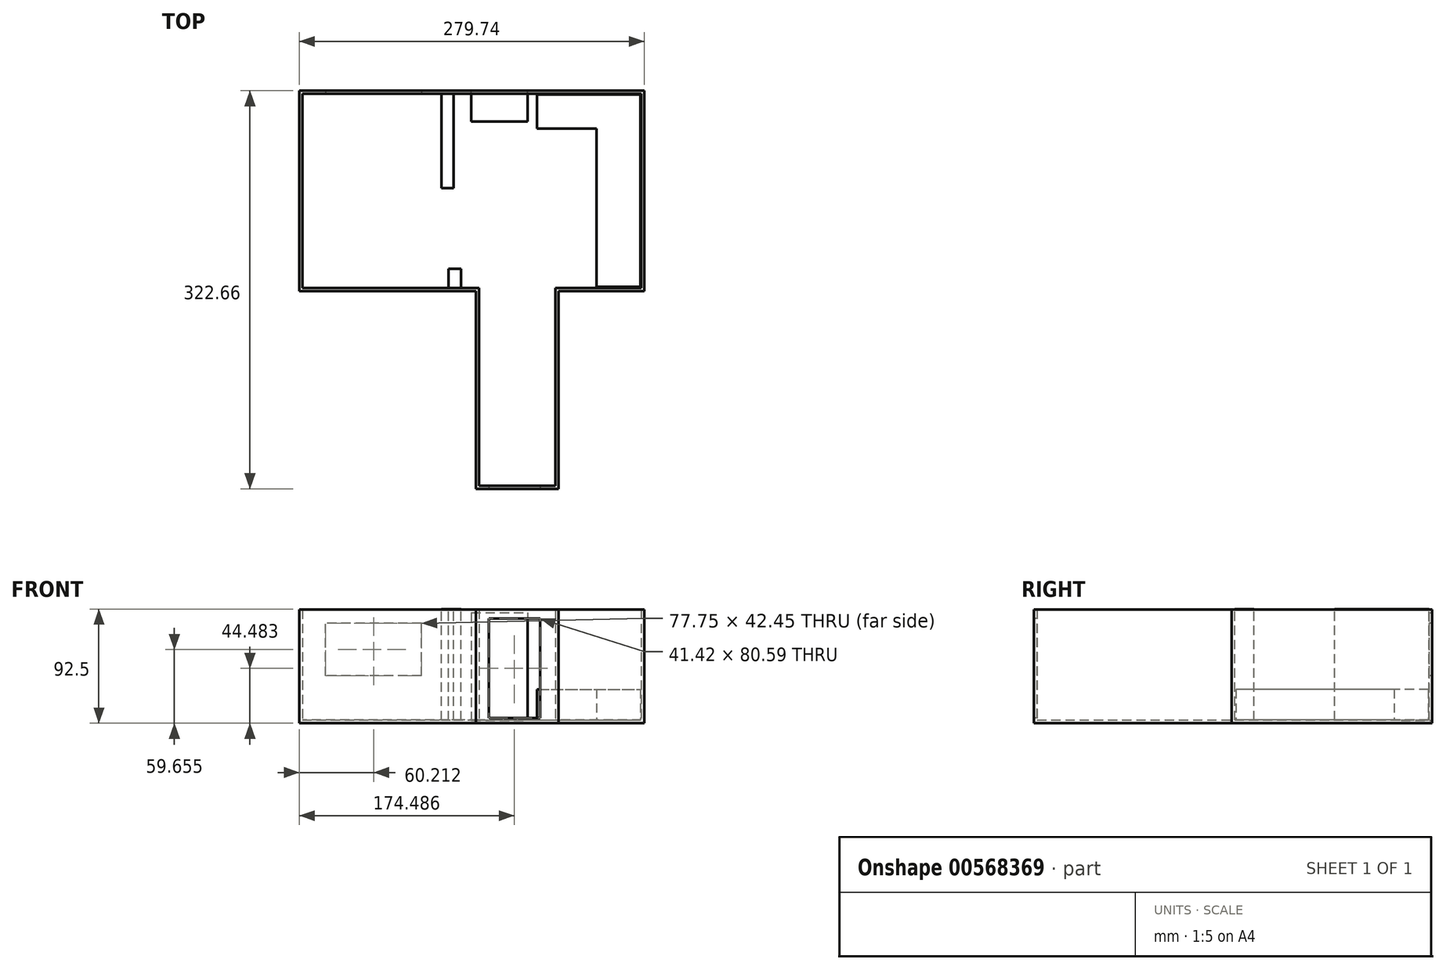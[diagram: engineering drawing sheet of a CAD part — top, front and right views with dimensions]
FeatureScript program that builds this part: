
annotation { "Feature Type Name" : "Feature", "Feature Type Description" : "" }
export const myFeature = defineFeature(function(context is Context, id is Id, definition is map)
    precondition{}
    {
        {
            var Q0;
            Q0=qCreatedBy(makeId("Top.planeOp"),FACE);
            var sketch = newSketch(context, id + "F0", { "sketchPlane" : qUnion([Q0])});
            skLineSegment(sketch, "E0", {"start": v(22.1, -110.4) * mm, "end": v(89.03, -110.4) * mm});
            skLineSegment(sketch, "E1", {"start": v(22.1, -110.4) * mm, "end": v(22.1, 49.82) * mm});
            skLineSegment(sketch, "E2", {"start": v(22.1, 49.82) * mm, "end": v(0, 49.82) * mm});
            skLineSegment(sketch, "E3", {"start": v(0, 49.82) * mm, "end": v(0, 72.95) * mm});
            skLineSegment(sketch, "E4", {"start": v(0, 49.82) * mm, "end": v(-121.09, 49.82) * mm});
            skLineSegment(sketch, "E5", {"start": v(-121.09, 49.82) * mm, "end": v(-121.09, 212.26) * mm});
            skLineSegment(sketch, "E6", {"start": v(-121.09, 212.26) * mm, "end": v(0, 212.26) * mm});
            skLineSegment(sketch, "E7", {"start": v(0, 212.26) * mm, "end": v(0, 116.46) * mm});
            skLineSegment(sketch, "E8", {"start": v(0, 212.26) * mm, "end": v(158.65, 212.26) * mm});
            skLineSegment(sketch, "E9", {"start": v(158.65, 212.26) * mm, "end": v(158.65, 49.82) * mm});
            skLineSegment(sketch, "E10", {"start": v(158.65, 49.82) * mm, "end": v(89.03, 49.82) * mm});
            skLineSegment(sketch, "E11", {"start": v(89.03, -110.4) * mm, "end": v(89.03, 49.82) * mm});
            skSolve(sketch);
        }
        {
            var Q0;
            Q0=makeQuery(id+"F0.imprint","IMPRINT",FACE,{"disambiguationData":[TD([[makeQuery(id+"F0.imprint","IMPRINT",EDGE,{"derivedFrom":sQuery(id+"F0.wireOp",EDGE,"E0")}),1.0]])]});
            extrude(context, id + "F1", {"entities" : qUnion([Q0]), "depth" : 92 * mm, "offsetDistance" : 25 * mm});
        }
        {
            var Q0;
            Q0=makeQuery(id+"F1.opExtrude","CAP_FACE",FACE,{"disambiguationData":[OSD([sQuery(id+"F0.wireOp",EDGE,"E0"),sQuery(id+"F0.wireOp",EDGE,"E1"),sQuery(id+"F0.wireOp",EDGE,"E2"),sQuery(id+"F0.wireOp",EDGE,"E4"),sQuery(id+"F0.wireOp",EDGE,"E5"),sQuery(id+"F0.wireOp",EDGE,"E6"),sQuery(id+"F0.wireOp",EDGE,"E8"),sQuery(id+"F0.wireOp",EDGE,"E9"),sQuery(id+"F0.wireOp",EDGE,"E10"),sQuery(id+"F0.wireOp",EDGE,"E11")])],"isStart":false});
            shell(context, id + "F2", {"entities" : qUnion([Q0]), "thickness" : 2.5 * mm});
        }
        {
            var Q0;
            Q0=makeQuery(id+"F2.opShell","OFFSET_FACE",FACE,{"disambiguationData":[OSD([sQuery(id+"F0.wireOp",EDGE,"E0"),sQuery(id+"F0.wireOp",EDGE,"E1"),sQuery(id+"F0.wireOp",EDGE,"E2"),sQuery(id+"F0.wireOp",EDGE,"E4"),sQuery(id+"F0.wireOp",EDGE,"E5"),sQuery(id+"F0.wireOp",EDGE,"E6"),sQuery(id+"F0.wireOp",EDGE,"E8"),sQuery(id+"F0.wireOp",EDGE,"E9"),sQuery(id+"F0.wireOp",EDGE,"E10"),sQuery(id+"F0.wireOp",EDGE,"E11")])]});
            var sketch = newSketch(context, id + "F3", { "sketchPlane" : qUnion([Q0])});
            skLineSegment(sketch, "E12", {"start": v(4.04, 52.32) * mm, "end": v(4.04, 89.94) * mm});
            skLineSegment(sketch, "E13", {"start": v(4.04, 209.76) * mm, "end": v(4.04, 133.28) * mm});
            skSolve(sketch);
        }
        {
            var Q0;
            Q0=sQuery(id+"F3.wireOp",EDGE,"E13");
            extrude(context, id + "F4", {"bodyType" : ToolBodyType.SURFACE, "surfaceEntities" : qUnion([Q0]), "depth" : 90 * mm, "offsetDistance" : 25 * mm});
        }
        {
            var Q0;
            Q0=makeQuery(id+"F4.opExtrude","SWEPT_FACE",FACE,{"disambiguationData":[OSD([sQuery(id+"F3.wireOp",EDGE,"E13")])]});
            extrude(context, id + "F5", {"entities" : qUnion([Q0]), "operationType" : NewBodyOperationType.ADD, "depth" : 10 * mm, "offsetDistance" : 25 * mm});
        }
        {
            var Q0;
            Q0=makeQuery(id+"F2.opShell","OFFSET_FACE",FACE,{"disambiguationData":[OSD([sQuery(id+"F0.wireOp",EDGE,"E0"),sQuery(id+"F0.wireOp",EDGE,"E1"),sQuery(id+"F0.wireOp",EDGE,"E2"),sQuery(id+"F0.wireOp",EDGE,"E4"),sQuery(id+"F0.wireOp",EDGE,"E5"),sQuery(id+"F0.wireOp",EDGE,"E6"),sQuery(id+"F0.wireOp",EDGE,"E8"),sQuery(id+"F0.wireOp",EDGE,"E9"),sQuery(id+"F0.wireOp",EDGE,"E10"),sQuery(id+"F0.wireOp",EDGE,"E11")])]});
            var sketch = newSketch(context, id + "F6", { "sketchPlane" : qUnion([Q0])});
            skLineSegment(sketch, "E14", {"start": v(0, 52.32) * mm, "end": v(0, 67.85) * mm});
            skSolve(sketch);
        }
        {
            var Q0;
            Q0=sQuery(id+"F6.wireOp",EDGE,"E14");
            extrude(context, id + "F7", {"bodyType" : ToolBodyType.SURFACE, "surfaceEntities" : qUnion([Q0]), "depth" : 90 * mm, "offsetDistance" : 25 * mm});
        }
        {
            var Q0;
            Q0=makeQuery(id+"F7.opExtrude","SWEPT_FACE",FACE,{"disambiguationData":[OSD([sQuery(id+"F6.wireOp",EDGE,"E14")])]});
            extrude(context, id + "F8", {"entities" : qUnion([Q0]), "operationType" : NewBodyOperationType.ADD, "depth" : 10 * mm, "offsetDistance" : 25 * mm});
        }
        {
            var Q0;
            Q0=makeQuery(id+"F1.opExtrude","SWEPT_FACE",FACE,{"disambiguationData":[OSD([sQuery(id+"F0.wireOp",EDGE,"E0")])]});
            var sketch = newSketch(context, id + "F9", { "sketchPlane" : qUnion([Q0])});
            skLineSegment(sketch, "E15", {"start": v(32.69, 84.78) * mm, "end": v(32.69, 4.19) * mm});
            skLineSegment(sketch, "E16", {"start": v(32.69, 4.19) * mm, "end": v(74.1, 4.19) * mm});
            skLineSegment(sketch, "E17", {"start": v(74.1, 4.19) * mm, "end": v(74.1, 84.78) * mm});
            skLineSegment(sketch, "E18", {"start": v(74.1, 84.78) * mm, "end": v(32.69, 84.78) * mm});
            skSolve(sketch);
        }
        {
            var Q0;
            Q0=makeQuery(id+"F9.imprint","IMPRINT",FACE,{"disambiguationData":[TD([[makeQuery(id+"F9.imprint","IMPRINT",EDGE,{"derivedFrom":sQuery(id+"F9.wireOp",EDGE,"E15")}),1.0]])]});
            extrude(context, id + "F10", {"entities" : qUnion([Q0]), "operationType" : NewBodyOperationType.REMOVE, "oppositeDirection" : true, "depth" : 25 * mm, "offsetDistance" : 25 * mm});
        }
        {
            var Q0;
            Q0=makeQuery(id+"F2.opShell","OFFSET_FACE",FACE,{"disambiguationData":[OSD([sQuery(id+"F0.wireOp",EDGE,"E0"),sQuery(id+"F0.wireOp",EDGE,"E1"),sQuery(id+"F0.wireOp",EDGE,"E2"),sQuery(id+"F0.wireOp",EDGE,"E4"),sQuery(id+"F0.wireOp",EDGE,"E5"),sQuery(id+"F0.wireOp",EDGE,"E6"),sQuery(id+"F0.wireOp",EDGE,"E8"),sQuery(id+"F0.wireOp",EDGE,"E9"),sQuery(id+"F0.wireOp",EDGE,"E10"),sQuery(id+"F0.wireOp",EDGE,"E11")])]});
            var sketch = newSketch(context, id + "F11", { "sketchPlane" : qUnion([Q0])});
            skPoint(sketch, "E19.0", {"position": v(-121.09, 212.26) * mm});
            skPoint(sketch, "E20.0", {"position": v(158.65, 212.26) * mm});
            skSolve(sketch);
        }
        {
            var Q0;
            Q0=makeQuery(id+"F1.opExtrude","SWEPT_FACE",FACE,{"disambiguationData":[OSD([sQuery(id+"F0.wireOp",EDGE,"E6"),sQuery(id+"F0.wireOp",EDGE,"E8")])]});
            var sketch = newSketch(context, id + "F12", { "sketchPlane" : qUnion([Q0])});
            skLineSegment(sketch, "E21.bottom", {"start": v(-18.47, 89.66) * mm, "end": v(-64, 89.66) * mm});
            skLineSegment(sketch, "E21.top", {"start": v(-18.47, 2.14) * mm, "end": v(-64, 2.14) * mm});
            skLineSegment(sketch, "E21.left", {"start": v(-18.47, 89.66) * mm, "end": v(-18.47, 2.14) * mm});
            skLineSegment(sketch, "E21.right", {"start": v(-64, 89.66) * mm, "end": v(-64, 2.14) * mm});
            skSolve(sketch);
        }
        {
            var Q0;
            Q0=makeQuery(id+"F12.imprint","IMPRINT",FACE,{"disambiguationData":[TD([[makeQuery(id+"F12.imprint","IMPRINT",EDGE,{"derivedFrom":sQuery(id+"F12.wireOp",EDGE,"E21.bottom")}),1.0]])]});
            extrude(context, id + "F13", {"entities" : qUnion([Q0]), "operationType" : NewBodyOperationType.REMOVE, "oppositeDirection" : true, "depth" : 25 * mm, "offsetDistance" : 25 * mm});
        }
        {
            var Q0;
            {var subQ0=sQuery(id+"F0.wireOp",EDGE,"E5");var subQ4=sQuery(id+"F0.wireOp",EDGE,"E8");var subQ5=sQuery(id+"F0.wireOp",EDGE,"E6");Q0=makeQuery(id+"F5.boolean.opBoolean","SPLIT",FACE,{"disambiguationData":[TD([makeQuery(id+"F2.opShell","OFFSET_FACE",FACE,{"disambiguationData":[OSD([subQ0])]})])],"derivedFrom":makeQuery(id+"F2.opShell","OFFSET_FACE",FACE,{"disambiguationData":[OSD([subQ5,subQ4])]})});}
            var sketch = newSketch(context, id + "F14", { "sketchPlane" : qUnion([Q0])});
            skLineSegment(sketch, "E22.bottom", {"start": v(-99.75, 80.88) * mm, "end": v(-22, 80.88) * mm});
            skLineSegment(sketch, "E22.top", {"start": v(-99.75, 38.43) * mm, "end": v(-22, 38.43) * mm});
            skLineSegment(sketch, "E22.left", {"start": v(-99.75, 80.88) * mm, "end": v(-99.75, 38.43) * mm});
            skLineSegment(sketch, "E22.right", {"start": v(-22, 80.88) * mm, "end": v(-22, 38.43) * mm});
            skSolve(sketch);
        }
        {
            var Q0;
            Q0 = qSketchRegion(id + "F14", true);
            extrude(context, id + "F15", {"entities" : qUnion([Q0]), "operationType" : NewBodyOperationType.REMOVE, "oppositeDirection" : true, "depth" : 25 * mm, "offsetDistance" : 25 * mm});
        }
        {
            var Q0;
            {var subQ9=sQuery(id+"F0.wireOp",EDGE,"E0");Q0=makeQuery(id+"F11.imprint","IMPRINT",FACE,{"disambiguationData":[TD([[makeQuery(id+"F11.imprint","IMPRINT",EDGE,{"derivedFrom":makeQuery(id+"F2.opShell","OFFSET_EDGE",EDGE,{"disambiguationData":[OSD([subQ9]),TDD([makeQuery(id+"F1.opExtrude","CAP_EDGE",EDGE,{"disambiguationData":[OSD([subQ9])],"isStart":true})])]})}),1.0]])]});}
            var sketch = newSketch(context, id + "F16", { "sketchPlane" : qUnion([Q0])});
            skLineSegment(sketch, "E23.bottom", {"start": v(71.67, 209.29) * mm, "end": v(155.45, 209.29) * mm});
            skLineSegment(sketch, "E23.top", {"start": v(71.67, 181.54) * mm, "end": v(155.45, 181.54) * mm});
            skLineSegment(sketch, "E23.left", {"start": v(71.67, 209.29) * mm, "end": v(71.67, 181.54) * mm});
            skLineSegment(sketch, "E23.right", {"start": v(155.45, 209.29) * mm, "end": v(155.45, 181.54) * mm});
            skLineSegment(sketch, "E24.bottom", {"start": v(120.07, 181.54) * mm, "end": v(155.45, 181.54) * mm});
            skLineSegment(sketch, "E24.top", {"start": v(120.07, 53.36) * mm, "end": v(155.45, 53.36) * mm});
            skLineSegment(sketch, "E24.left", {"start": v(120.07, 181.54) * mm, "end": v(120.07, 53.36) * mm});
            skLineSegment(sketch, "E24.right", {"start": v(155.45, 181.54) * mm, "end": v(155.45, 53.36) * mm});
            skSolve(sketch);
        }
        {
            var Q0;
            Q0 = qSketchRegion(id + "F16", true);
            extrude(context, id + "F17", {"entities" : qUnion([Q0]), "operationType" : NewBodyOperationType.ADD, "depth" : 25 * mm, "offsetDistance" : 25 * mm});
        }
    });
